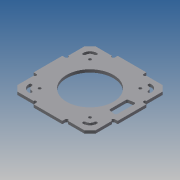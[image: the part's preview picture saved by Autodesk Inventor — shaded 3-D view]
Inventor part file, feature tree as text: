
AUTODESK INVENTOR PART (.ipt)
format: ipt  version: 2017 (Build 210142000, 142)  size: 166,400 bytes
history: native  units: mm
features: other x4, extrude x1, reference x1
ambient origin geometry x8: Origin, YZ Plane, XZ Plane, XY Plane, X Axis, Y Axis, Z Axis, Center Point
bodies: Body1 (feature_tree)
feature tree (6):
  other  "Sólido1"
  extrude  "Extrusión1"  Depth=70.0mm
  reference  "Referencia2"
  other  "<userpath>\Documents\GitHub\actor-re-actor\models\inventor-caja\Case\Case-D.iam"
  other  "Case-D.iam"
  other  "Tapa Enchufes b:1"
